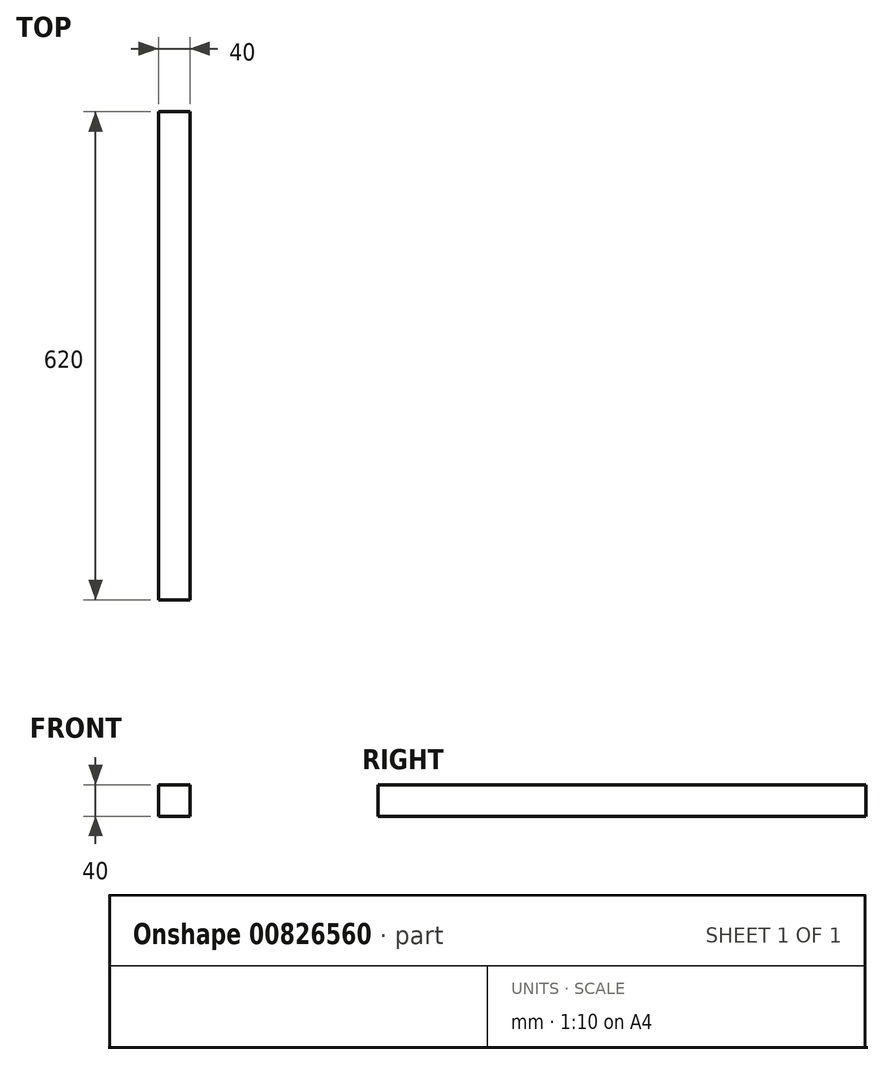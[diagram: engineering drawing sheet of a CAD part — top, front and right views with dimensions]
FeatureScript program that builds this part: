
annotation { "Feature Type Name" : "Feature", "Feature Type Description" : "" }
export const myFeature = defineFeature(function(context is Context, id is Id, definition is map)
    precondition{}
    {
        {
            var Q0;
            Q0=qCreatedBy(makeId("Front.planeOp"),FACE);
            var sketch = newSketch(context, id + "F0", { "sketchPlane" : qUnion([Q0])});
            skLineSegment(sketch, "E0.bottom", {"start": v(20, -20) * mm, "end": v(-20, -20) * mm});
            skLineSegment(sketch, "E0.top", {"start": v(20, 20) * mm, "end": v(-20, 20) * mm});
            skLineSegment(sketch, "E0.left", {"start": v(20, -20) * mm, "end": v(20, 20) * mm});
            skLineSegment(sketch, "E0.right", {"start": v(-20, -20) * mm, "end": v(-20, 20) * mm});
            skPoint(sketch, "E0.middle", {"position": v(0, 0) * mm});
            skSolve(sketch);
        }
        {
            var Q0;
            Q0=makeQuery(id+"F0.imprint","IMPRINT",FACE,{"disambiguationData":[TD([[makeQuery(id+"F0.imprint","IMPRINT",EDGE,{"derivedFrom":sQuery(id+"F0.wireOp",EDGE,"E0.bottom")}),-1.0]])]});
            extrude(context, id + "F1", {"entities" : qUnion([Q0]), "depth" : 620 * mm, "offsetDistance" : 25.4 * mm});
        }
    });
